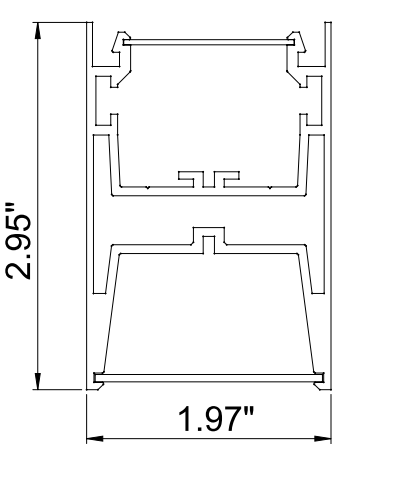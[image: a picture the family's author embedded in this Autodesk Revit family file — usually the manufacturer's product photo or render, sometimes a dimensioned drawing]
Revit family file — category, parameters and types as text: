
# Revit family: BX - CURV SERIES
name_source: partatom
category: Lighting Fixtures
units: mm (PartAtom-declared; Revit-internal decimal feet)

## family parameters
Cut with Voids When Loaded = No
Host = Face
Light Source = No
Part Type = Normal
Room Calculation Point = No
Round Connector Dimension = Use Diameter
Shared = No

## types (3) — shared parameters
Apparent Load = 0 VA
Description = Indoor Architectural LED Fixture. Pendant, Surface, Wall Mounted & Recessed Installation.
Distribution = Direct
Driver Options = 0-10V Dimming
FINISH = Aluminum
FIXTURE ID = CURV SERIES
Lamp = LED
Light Height = 2.95 "
Light Length = 24 "
Light Width = 1.97 "
Lumens = 2000 lm
MOUNTING = Pendant
Manufacturer = techoLED
Model = TechoLED-BX-CURV
Pendant Length = 15 "
Rdwn = 8
Type Comments = CURV SERIES
URL = https://techoled.com
Voltage = 277 V
zero-valued in all types: Default Elevation

## per-type parameters (varying)
| type | Actual Bend Radius 2 | Actual Degree | Bend Radius | L1 | L2 |
| 59.06" Radius | 60.05 " | 23.28° | 59.06 " | 58.88 " | 55.89 " |
| 98.43" Radius | 99.42 " | 13.97° | 98.43 " | 98.25 " | 98 " |
| 188.98" Radius | 189.97 " | 7.28° | 188.98 " | 188.8 " | 188.63 " |

## geometry (parser evidence)
native form markers: Sweep x29
no freeform markers — native parametric forms only
